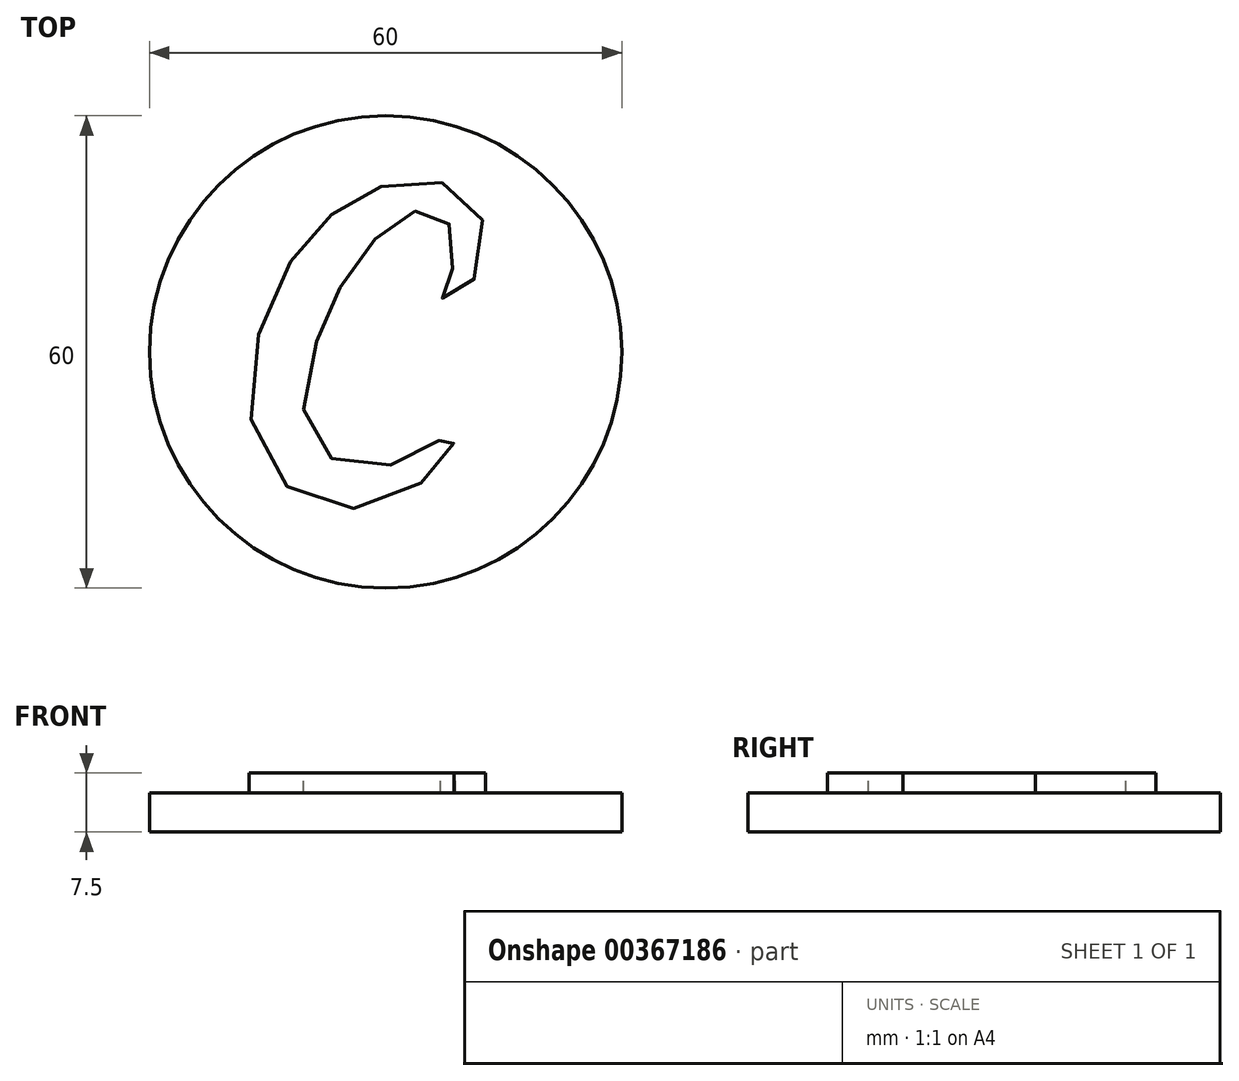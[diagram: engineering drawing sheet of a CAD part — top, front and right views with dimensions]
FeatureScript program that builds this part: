
annotation { "Feature Type Name" : "Feature", "Feature Type Description" : "" }
export const myFeature = defineFeature(function(context is Context, id is Id, definition is map)
    precondition{}
    {
        {
            var Q0;
            Q0=qCreatedBy(makeId("Top.planeOp"),FACE);
            var sketch = newSketch(context, id + "F0", { "sketchPlane" : qUnion([Q0])});
            skCircle(sketch, "E0", {"center": v(0, 0) * mm, "radius": 30 * mm});
            skCircle(sketch, "E1", {"center": v(0, 0) * mm, "radius": 37 * mm});
            skCircle(sketch, "E2", {"center": v(0, 0) * mm, "radius": 45 * mm});
            skCircle(sketch, "E3", {"center": v(0, 0) * mm, "radius": 53 * mm});
            skPoint(sketch, "E4", {"position": v(-10.7, 16.8) * mm});
            skPoint(sketch, "E5", {"position": v(-11.88, 15.26) * mm});
            skPoint(sketch, "E6", {"position": v(-13.2, 13.15) * mm});
            skPoint(sketch, "E7", {"position": v(-14.5, 10.83) * mm});
            skPoint(sketch, "E8", {"position": v(-15.69, 8.42) * mm});
            skPoint(sketch, "E9", {"position": v(-16.69, 5.59) * mm});
            skPoint(sketch, "E10", {"position": v(-17.58, 3.07) * mm});
            skPoint(sketch, "E11", {"position": v(-18.15, 0.87) * mm});
            skPoint(sketch, "E12", {"position": v(-18.66, -1.67) * mm});
            skPoint(sketch, "E13", {"position": v(-18.81, -3.94) * mm});
            skPoint(sketch, "E14", {"position": v(-18.87, -5.57) * mm});
            skPoint(sketch, "E15", {"position": v(-18.87, -7.9) * mm});
            skPoint(sketch, "E16", {"position": v(-18.75, -9.9) * mm});
            skPoint(sketch, "E17", {"position": v(-18.5, -12.04) * mm});
            skPoint(sketch, "E18", {"position": v(-17.96, -13.84) * mm});
            skPoint(sketch, "E19", {"position": v(-16.95, -15.53) * mm});
            skPoint(sketch, "E20", {"position": v(-15.69, -17.13) * mm});
            skPoint(sketch, "E21", {"position": v(-14.18, -18.56) * mm});
            skPoint(sketch, "E22", {"position": v(-12.44, -19.97) * mm});
            skPoint(sketch, "E23", {"position": v(-10.83, -20.99) * mm});
            skPoint(sketch, "E24", {"position": v(-8.7, -21.57) * mm});
            skPoint(sketch, "E25", {"position": v(-6.55, -21.91) * mm});
            skPoint(sketch, "E26", {"position": v(-4.42, -22.09) * mm});
            skPoint(sketch, "E27", {"position": v(-2.22, -21.86) * mm});
            skPoint(sketch, "E28", {"position": v(-0.67, -21.56) * mm});
            skPoint(sketch, "E29", {"position": v(1.27, -20.99) * mm});
            skPoint(sketch, "E30", {"position": v(2.86, -19.97) * mm});
            skPoint(sketch, "E31", {"position": v(4.36, -18.85) * mm});
            skPoint(sketch, "E32", {"position": v(5.74, -17.76) * mm});
            skPoint(sketch, "E33", {"position": v(7.31, -16.5) * mm});
            skPoint(sketch, "E34", {"position": v(8.41, -15.53) * mm});
            skPoint(sketch, "E35", {"position": v(9.33, -13.84) * mm});
            skPoint(sketch, "E36", {"position": v(9.65, -12.3) * mm});
            skPoint(sketch, "E37", {"position": v(9.54, -11.65) * mm});
            skPoint(sketch, "E38", {"position": v(8.41, -11.7) * mm});
            skPoint(sketch, "E39", {"position": v(7.7, -12.3) * mm});
            skPoint(sketch, "E40", {"position": v(6.8, -13.06) * mm});
            skPoint(sketch, "E41", {"position": v(5.74, -13.84) * mm});
            skPoint(sketch, "E42", {"position": v(4.36, -14.52) * mm});
            skPoint(sketch, "E43", {"position": v(2.86, -15.04) * mm});
            skPoint(sketch, "E44", {"position": v(1.27, -15.53) * mm});
            skPoint(sketch, "E45", {"position": v(0, -15.8) * mm});
            skPoint(sketch, "E46", {"position": v(-1.58, -16.07) * mm});
            skPoint(sketch, "E47", {"position": v(-3.16, -16.2) * mm});
            skPoint(sketch, "E48", {"position": v(-4.97, -16.2) * mm});
            skPoint(sketch, "E49", {"position": v(-6.55, -15.73) * mm});
            skPoint(sketch, "E50", {"position": v(-7.94, -15) * mm});
            skPoint(sketch, "E51", {"position": v(-9.29, -13.84) * mm});
            skPoint(sketch, "E52", {"position": v(-10.4, -12.14) * mm});
            skPoint(sketch, "E53", {"position": v(-11.3, -10.3) * mm});
            skPoint(sketch, "E54", {"position": v(-11.37, -8.13) * mm});
            skPoint(sketch, "E55", {"position": v(-11.14, -5.57) * mm});
            skPoint(sketch, "E56", {"position": v(-10.83, -3.1) * mm});
            skPoint(sketch, "E57", {"position": v(-10.35, -1.02) * mm});
            skPoint(sketch, "E58", {"position": v(-9.68, 0.8) * mm});
            skPoint(sketch, "E59", {"position": v(-9.03, 2.87) * mm});
            skPoint(sketch, "E60", {"position": v(-8.1, 4.94) * mm});
            skPoint(sketch, "E61", {"position": v(-7.29, 6.74) * mm});
            skPoint(sketch, "E62", {"position": v(-6.36, 8.54) * mm});
            skPoint(sketch, "E63", {"position": v(-5.43, 10.29) * mm});
            skPoint(sketch, "E64", {"position": v(-4.34, 11.81) * mm});
            skPoint(sketch, "E65", {"position": v(-3.09, 13.5) * mm});
            skPoint(sketch, "E66", {"position": v(-1.94, 15.03) * mm});
            skPoint(sketch, "E67", {"position": v(-0.74, 16.23) * mm});
            skPoint(sketch, "E68", {"position": v(0.74, 17.74) * mm});
            skPoint(sketch, "E69", {"position": v(2.25, 18.95) * mm});
            skPoint(sketch, "E70", {"position": v(3.78, 19.66) * mm});
            skPoint(sketch, "E71", {"position": v(5.47, 19.83) * mm});
            skPoint(sketch, "E72", {"position": v(7.39, 19.26) * mm});
            skPoint(sketch, "E73", {"position": v(8.36, 18.22) * mm});
            skPoint(sketch, "E74", {"position": v(9.03, 16.7) * mm});
            skPoint(sketch, "E75", {"position": v(9.31, 15.34) * mm});
            skPoint(sketch, "E76", {"position": v(9.34, 13.51) * mm});
            skPoint(sketch, "E77", {"position": v(9.07, 12.09) * mm});
            skPoint(sketch, "E78", {"position": v(8.4, 10.31) * mm});
            skPoint(sketch, "E79", {"position": v(7.49, 8.92) * mm});
            skPoint(sketch, "E80", {"position": v(7.38, 7.89) * mm});
            skPoint(sketch, "E81", {"position": v(8.25, 7.23) * mm});
            skPoint(sketch, "E82", {"position": v(9.45, 7.29) * mm});
            skPoint(sketch, "E83", {"position": v(10.7, 7.89) * mm});
            skPoint(sketch, "E84", {"position": v(11.86, 9) * mm});
            skPoint(sketch, "E85", {"position": v(12.88, 10.34) * mm});
            skPoint(sketch, "E86", {"position": v(13.87, 12.25) * mm});
            skPoint(sketch, "E87", {"position": v(14.36, 14.7) * mm});
            skPoint(sketch, "E88", {"position": v(14.36, 16.64) * mm});
            skPoint(sketch, "E89", {"position": v(14.18, 18.56) * mm});
            skPoint(sketch, "E90", {"position": v(13.43, 20.5) * mm});
            skPoint(sketch, "E91", {"position": v(12.25, 21.78) * mm});
            skPoint(sketch, "E92", {"position": v(11.22, 22.56) * mm});
            skPoint(sketch, "E93", {"position": v(9.68, 23.17) * mm});
            skPoint(sketch, "E94", {"position": v(8.07, 23.66) * mm});
            skPoint(sketch, "E95", {"position": v(6.24, 23.81) * mm});
            skPoint(sketch, "E96", {"position": v(4.37, 23.78) * mm});
            skPoint(sketch, "E97", {"position": v(1.9, 23.54) * mm});
            skPoint(sketch, "E98", {"position": v(0, 23.17) * mm});
            skPoint(sketch, "E99", {"position": v(-2.26, 22.56) * mm});
            skPoint(sketch, "E100", {"position": v(-3.96, 21.78) * mm});
            skPoint(sketch, "E101", {"position": v(-5.35, 20.9) * mm});
            skPoint(sketch, "E102", {"position": v(-6.84, 19.93) * mm});
            skPoint(sketch, "E103", {"position": v(-8.33, 18.85) * mm});
            skPoint(sketch, "E104", {"position": v(-9.62, 17.77) * mm});
            skFitSpline(sketch, "E105", {"points": [v(8.25, 7.23) * mm, v(9.45, 7.29) * mm, v(10.7, 7.89) * mm, v(11.86, 9) * mm, v(12.88, 10.34) * mm, v(13.87, 12.25) * mm, v(14.36, 14.7) * mm, v(14.36, 16.64) * mm, v(14.18, 18.56) * mm, v(13.43, 20.5) * mm, v(12.25, 21.78) * mm, v(11.22, 22.56) * mm, v(9.68, 23.17) * mm, v(8.07, 23.66) * mm, v(6.24, 23.81) * mm, v(4.37, 23.78) * mm, v(1.9, 23.54) * mm, v(0, 23.17) * mm, v(-2.26, 22.56) * mm, v(-3.96, 21.78) * mm, v(-5.35, 20.9) * mm, v(-6.84, 19.93) * mm, v(-8.33, 18.85) * mm, v(-9.62, 17.77) * mm, v(-10.7, 16.8) * mm, v(-11.88, 15.26) * mm, v(-13.2, 13.15) * mm, v(-14.5, 10.83) * mm, v(-15.69, 8.42) * mm, v(-16.69, 5.59) * mm, v(-17.58, 3.07) * mm, v(-18.15, 0.87) * mm, v(-18.66, -1.67) * mm, v(-18.81, -3.94) * mm, v(-18.87, -5.57) * mm, v(-18.87, -7.9) * mm, v(-18.75, -9.9) * mm, v(-18.5, -12.04) * mm, v(-17.96, -13.84) * mm, v(-16.95, -15.53) * mm, v(-15.69, -17.13) * mm, v(-14.18, -18.56) * mm, v(-12.44, -19.97) * mm, v(-10.83, -20.99) * mm, v(-8.7, -21.57) * mm, v(-6.55, -21.91) * mm, v(-4.42, -22.09) * mm, v(-2.22, -21.86) * mm, v(-0.67, -21.56) * mm, v(1.27, -20.99) * mm, v(2.86, -19.97) * mm, v(4.36, -18.85) * mm, v(5.74, -17.76) * mm, v(7.31, -16.5) * mm, v(8.41, -15.53) * mm, v(9.33, -13.84) * mm, v(9.65, -12.3) * mm, v(9.54, -11.65) * mm, v(8.98, -11.45) * mm, v(8.41, -11.7) * mm, v(7.7, -12.3) * mm, v(6.8, -13.06) * mm, v(5.74, -13.84) * mm, v(4.36, -14.52) * mm, v(2.86, -15.04) * mm, v(1.27, -15.53) * mm, v(0, -15.8) * mm, v(-1.58, -16.07) * mm, v(-3.16, -16.2) * mm, v(-4.97, -16.2) * mm, v(-6.55, -15.73) * mm, v(-7.94, -15) * mm, v(-9.29, -13.84) * mm, v(-10.4, -12.14) * mm, v(-11.3, -10.3) * mm, v(-11.37, -8.13) * mm, v(-11.14, -5.57) * mm, v(-10.83, -3.1) * mm, v(-10.35, -1.02) * mm, v(-9.68, 0.8) * mm, v(-9.03, 2.87) * mm, v(-8.1, 4.94) * mm, v(-7.29, 6.74) * mm, v(-6.36, 8.54) * mm, v(-5.43, 10.29) * mm, v(-4.34, 11.81) * mm, v(-3.09, 13.5) * mm, v(-1.94, 15.03) * mm, v(-0.74, 16.23) * mm, v(0.74, 17.74) * mm, v(2.25, 18.95) * mm, v(3.78, 19.66) * mm, v(5.47, 19.83) * mm, v(7.39, 19.26) * mm, v(8.36, 18.22) * mm, v(9.03, 16.7) * mm, v(9.31, 15.34) * mm, v(9.34, 13.51) * mm, v(9.07, 12.09) * mm, v(8.4, 10.31) * mm, v(7.49, 8.92) * mm, v(7.38, 7.89) * mm, v(8.25, 7.23) * mm]});
            skSolve(sketch);
        }
        {
            var Q0;
            Q0=qCreatedBy(makeId("Top.planeOp"),FACE);
            var sketch = newSketch(context, id + "F1", { "sketchPlane" : qUnion([Q0])});
            skFitSpline(sketch, "E106", {"points": [v(-6.89, 17.44) * mm, v(-13.78, 8.39) * mm, v(-16.83, -10.03) * mm, v(-7.37, -19.7) * mm, v(5.3, -16.02) * mm, v(8.67, -11.16) * mm, v(8.15, -10.33) * mm, v(5.77, -12.05) * mm, v(-2.94, -14.66) * mm, v(-9.85, -10.23) * mm, v(-8.75, 1.47) * mm, v(-4.8, 9.75) * mm, v(1.15, 16.63) * mm, v(5.44, 17.94) * mm, v(8.43, 15.58) * mm, v(8.25, 9.93) * mm, v(6.96, 7.27) * mm, v(8.1, 6.57) * mm, v(12.34, 11.66) * mm, v(10.1, 20.1) * mm, v(0.95, 21.42) * mm, v(-6.89, 17.44) * mm]});
            skCircle(sketch, "E107", {"center": v(0, 0) * mm, "radius": 30 * mm});
            skCircle(sketch, "E108", {"center": v(0, 0) * mm, "radius": 37 * mm});
            skCircle(sketch, "E109", {"center": v(0, 0) * mm, "radius": 45 * mm});
            skCircle(sketch, "E110", {"center": v(0, 0) * mm, "radius": 53 * mm});
            skSolve(sketch);
        }
        {
            var Q0;
            Q0=makeQuery(id+"F1.imprint","IMPRINT",FACE,{"disambiguationData":[TD([[makeQuery(id+"F1.imprint","IMPRINT",EDGE,{"derivedFrom":sQuery(id+"F1.wireOp",EDGE,"E106")}),1.0]])]});
            extrude(context, id + "F2", {"entities" : qUnion([Q0]), "depth" : 7.5 * mm});
        }
        {
            var Q0;
            Q0=makeQuery(id+"F1.imprint","IMPRINT",FACE,{"disambiguationData":[TD([[makeQuery(id+"F1.imprint","IMPRINT",EDGE,{"derivedFrom":sQuery(id+"F1.wireOp",EDGE,"E106")}),-1.0]])]});
            extrude(context, id + "F3", {"entities" : qUnion([Q0]), "operationType" : NewBodyOperationType.ADD, "depth" : 5 * mm});
        }
    });
